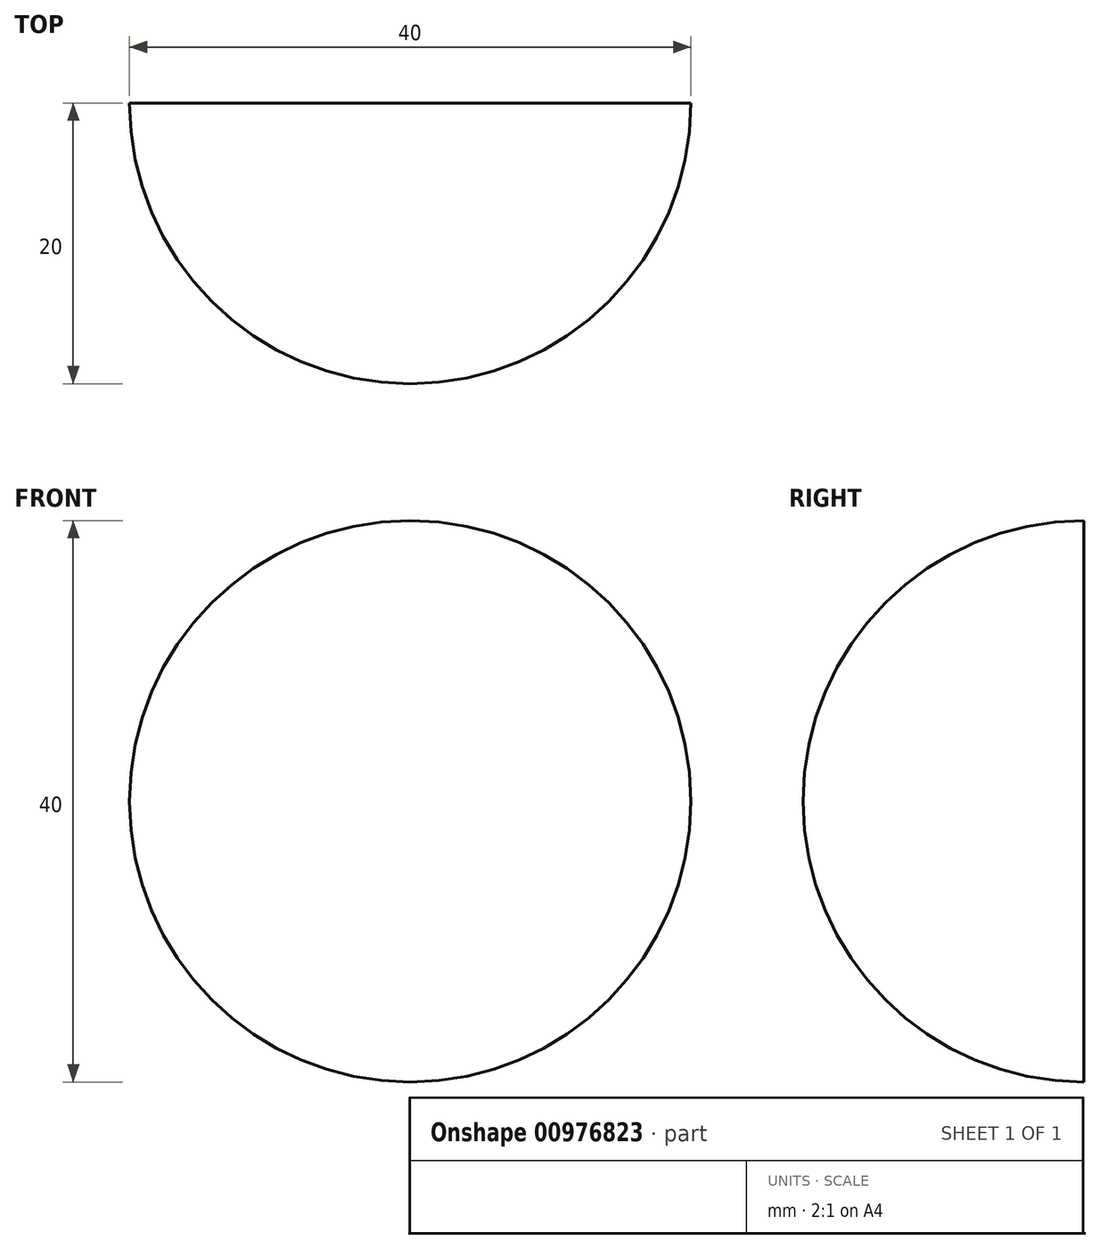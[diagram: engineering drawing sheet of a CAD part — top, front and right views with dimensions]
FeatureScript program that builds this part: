
annotation { "Feature Type Name" : "Feature", "Feature Type Description" : "" }
export const myFeature = defineFeature(function(context is Context, id is Id, definition is map)
    precondition{}
    {
        {
            var Q0;
            Q0=qCreatedBy(makeId("Front.planeOp"),FACE);
            var sketch = newSketch(context, id + "F0", { "sketchPlane" : qUnion([Q0])});
            skLineSegment(sketch, "E0", {"start": v(0, 0) * mm, "end": v(0, 20) * mm});
            skCircle(sketch, "E1", {"center": v(0, 0) * mm, "radius": 20 * mm});
            skLineSegment(sketch, "E2", {"start": v(0, 0) * mm, "end": v(0, -20) * mm});
            skSolve(sketch);
        }
        {
            var Q0;
            Q0=qCreatedBy(makeId("Front.planeOp"),FACE);
            var sketch = newSketch(context, id + "F1", { "sketchPlane" : qUnion([Q0])});
            skLineSegment(sketch, "E3", {"start": v(0, 0) * mm, "end": v(0, 19) * mm});
            skLineSegment(sketch, "E4", {"start": v(0, 0) * mm, "end": v(-19, 0) * mm});
            skLineSegment(sketch, "E5.0", {"start": v(-0.75, 0.75) * mm, "end": v(-0.75, 19) * mm});
            skLineSegment(sketch, "E5.1", {"start": v(-0.75, 0.75) * mm, "end": v(-19, 0.75) * mm});
            skLineSegment(sketch, "E6.1.0", {"start": v(-0.75, -0.75) * mm, "end": v(-19, -0.75) * mm});
            skLineSegment(sketch, "E6.1.1", {"start": v(-0.75, -0.75) * mm, "end": v(-0.75, -19) * mm});
            skLineSegment(sketch, "E6.2.0", {"start": v(0.75, -0.75) * mm, "end": v(0.75, -19) * mm});
            skLineSegment(sketch, "E6.2.1", {"start": v(0.75, -0.75) * mm, "end": v(19, -0.75) * mm});
            skLineSegment(sketch, "E6.3.0", {"start": v(0.75, 0.75) * mm, "end": v(19, 0.75) * mm});
            skLineSegment(sketch, "E6.3.1", {"start": v(0.75, 0.75) * mm, "end": v(0.75, 19) * mm});
            skPoint(sketch, "E6.center", {"position": v(0, 0) * mm});
            skLineSegment(sketch, "E7", {"start": v(0.75, 19) * mm, "end": v(-0.75, 19) * mm});
            skLineSegment(sketch, "E8", {"start": v(-19, 0.75) * mm, "end": v(-19, -0.75) * mm});
            skLineSegment(sketch, "E9", {"start": v(-0.75, -19) * mm, "end": v(0.75, -19) * mm});
            skLineSegment(sketch, "E10", {"start": v(19, -0.75) * mm, "end": v(19, 0.75) * mm});
            skSolve(sketch);
        }
        {
            var Q0;
            {var subQ4=sQuery(id+"F1.wireOp",EDGE,"E3");Q0=makeQuery(id+"F1.imprint","IMPRINT",FACE,{"disambiguationData":[TD([[makeQuery(id+"F1.imprint","IMPRINT",EDGE,{"derivedFrom":subQ4}),-1.0]])]});}
            var Q1;
            {var subQ4=sQuery(id+"F1.wireOp",EDGE,"E3");Q1=makeQuery(id+"F1.imprint","IMPRINT",FACE,{"disambiguationData":[TD([[makeQuery(id+"F1.imprint","IMPRINT",EDGE,{"derivedFrom":subQ4}),1.0]])]});}
            extrude(context, id + "F2", {"entities" : qUnion([Q0, Q1]), "depth" : 24.5 * mm, "offsetDistance" : 25 * mm});
        }
        {
            var Q0;
            {var subQ0=sQuery(id+"F0.wireOp",EDGE,"E1");var subQ1=sQuery(id+"F0.wireOp",EDGE,"E0");var subQ2=makeQuery(id+"F0.imprint","INTERSECT",VERTEX,{"derivedFrom":[subQ1,subQ0]});Q0=makeQuery(id+"F0.imprint","IMPRINT",FACE,{"disambiguationData":[TD([[makeQuery(id+"F0.imprint","IMPRINT",EDGE,{"disambiguationData":[TD([[subQ2,1.0]])],"derivedFrom":subQ1}),1.0]])]});}
            var Q1;
            Q1=sQuery(id+"F0.wireOp",EDGE,"E0");
            revolve(context, id + "F3", {"surfaceOperationType" : NewSurfaceOperationType.NEW, "entities" : qUnion([Q0]), "axis" : qUnion([Q1]), "revolveType" : RevolveType.ONE_DIRECTION, "angle" : 180 * degree});
        }
        {
            var Q0;
            Q0=makeQuery(id+"F3.opRevolve","SWEPT_BODY",BODY,{"disambiguationData":[OSD([sQuery(id+"F0.wireOp",EDGE,"E0"),sQuery(id+"F0.wireOp",EDGE,"E1"),sQuery(id+"F0.wireOp",EDGE,"58411db6-5779-4326-ab1f-40945c4c65a3.0"),sQuery(id+"F0.wireOp",EDGE,"E2")])]});
            var Q1;
            Q1=makeQuery(id+"F2.opExtrude","SWEPT_BODY",BODY,{"disambiguationData":[OSD([sQuery(id+"F1.wireOp",EDGE,"E5.0"),sQuery(id+"F1.wireOp",EDGE,"E5.1"),sQuery(id+"F1.wireOp",EDGE,"E6.1.0"),sQuery(id+"F1.wireOp",EDGE,"E6.1.1"),sQuery(id+"F1.wireOp",EDGE,"E6.2.0"),sQuery(id+"F1.wireOp",EDGE,"E6.2.1"),sQuery(id+"F1.wireOp",EDGE,"E6.3.0"),sQuery(id+"F1.wireOp",EDGE,"E6.3.1"),sQuery(id+"F1.wireOp",EDGE,"E7"),sQuery(id+"F1.wireOp",EDGE,"E8"),sQuery(id+"F1.wireOp",EDGE,"E9"),sQuery(id+"F1.wireOp",EDGE,"E10")])]});
            booleanBodies(context, id + "F4", {"operationType" : BooleanOperationType.SUBTRACTION, "tools" : qUnion([Q0]), "targets" : qUnion([Q1]), "keepTools" : true});
        }
        {
            var Q0;
            Q0=makeQuery(id+"F4.opBoolean","SPLIT",BODY,{"disambiguationData":[OD(0.0)],"derivedFrom":makeQuery(id+"F2.opExtrude","SWEPT_BODY",BODY,{"disambiguationData":[OSD([sQuery(id+"F1.wireOp",EDGE,"E5.0"),sQuery(id+"F1.wireOp",EDGE,"E5.1"),sQuery(id+"F1.wireOp",EDGE,"E6.1.0"),sQuery(id+"F1.wireOp",EDGE,"E6.1.1"),sQuery(id+"F1.wireOp",EDGE,"E6.2.0"),sQuery(id+"F1.wireOp",EDGE,"E6.2.1"),sQuery(id+"F1.wireOp",EDGE,"E6.3.0"),sQuery(id+"F1.wireOp",EDGE,"E6.3.1"),sQuery(id+"F1.wireOp",EDGE,"E7"),sQuery(id+"F1.wireOp",EDGE,"E8"),sQuery(id+"F1.wireOp",EDGE,"E9"),sQuery(id+"F1.wireOp",EDGE,"E10")])]})});
            deleteBodies(context, id + "F5", {"entities" : qUnion([Q0])});
        }
    });
